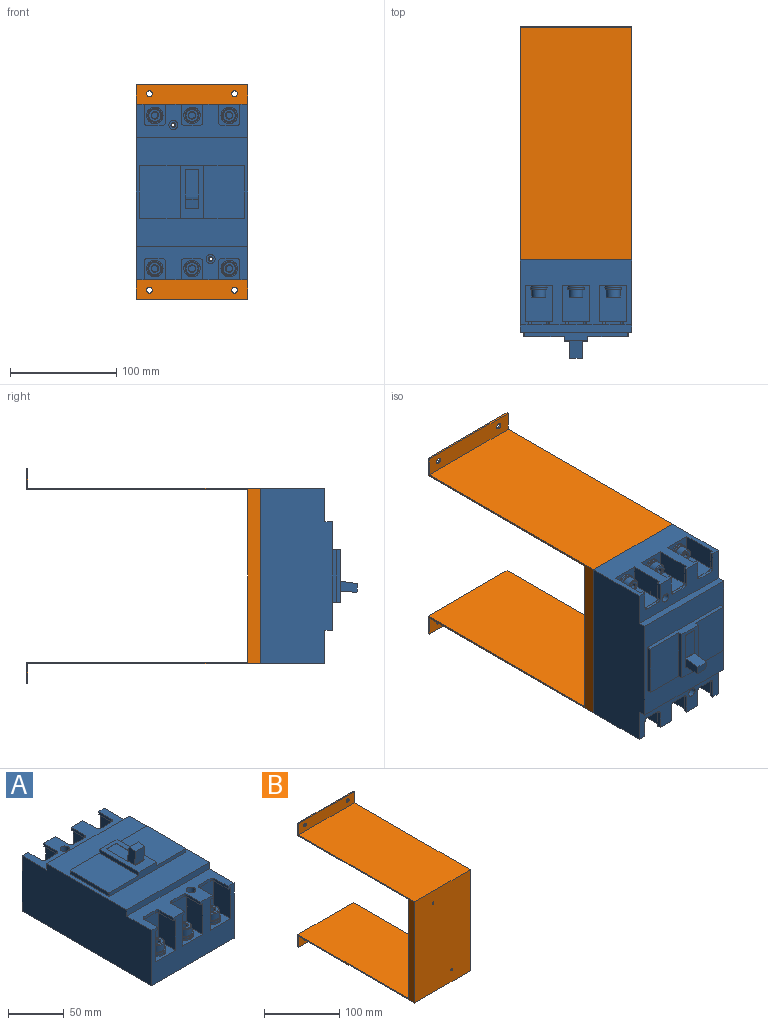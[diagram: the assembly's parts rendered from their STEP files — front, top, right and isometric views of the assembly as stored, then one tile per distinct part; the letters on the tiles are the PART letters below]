
ASSEMBLY  parts=2 mates=1
PART A: 239 faces, bbox 105x165x92 mm
  f0: plane 49x4mm, normal (1,0,0), area 196mm2, adj f1,f7,f8,f222
  f1: plane 4x0.5mm, normal (0.71,-0.71,0), area 2.8mm2, adj f0,f5,f7,f222
  f2: plane 49x4mm, normal (-1,0,0), area 196mm2, adj f3,f4,f222,f223
  f3: plane 50x38mm, normal (0,0,1), area 1899.8mm2, adj f2,f4,f5,f223,f224,f225
  f4: plane 4x0.5mm, normal (-0.71,-0.71,0), area 2.8mm2, adj f2,f3,f5,f222
  f5: plane 97x8mm, normal (0,-1,0), area 476mm2, adj f1,f3,f4,f6,f7,f222,f225,f226
  f6: plane 50x4mm, normal (1,0,0), area 200mm2, adj f5,f7,f224,f226
  f7: plane 50x38mm, normal (0,0,1), area 1899.8mm2, adj f0,f1,f5,f6,f8,f224
  f8: plane 4x0.5mm, normal (0.71,0.71,0), area 2.8mm2, adj f0,f7,f222,f224
  f9: plane 6.93x6mm, normal (0,0,1), area 31.2mm2, adj f10,f11,f12,f13,f14,f15
  f10: plane 6.98x3mm, normal (-0.5,0.87,0), area 23.1mm2, adj f9,f11,f15,f16
  f11: plane 6.98x3.46mm, normal (-1,0,0), area 23.1mm2, adj f9,f10,f12,f16
  f12: plane 6.98x3mm, normal (-0.5,-0.87,0), area 23.1mm2, adj f9,f11,f13,f16
  f13: plane 6.98x3mm, normal (0.5,-0.87,0), area 23.1mm2, adj f9,f12,f14,f16
  f14: plane 6.98x3.46mm, normal (1,0,0), area 23.1mm2, adj f9,f13,f15,f16
  f15: plane 6.98x3mm, normal (0.5,0.87,0), area 23.1mm2, adj f9,f10,f14,f16
  f16: cone r=2.46mm half-angle=45deg, axis (0,0,1), area 9.7mm2, adj f10,f11,f12,f13,f14,f15,f17
  f17: plane 11.4x11.4mm, normal (0,0,1), area 64mm2, adj f16,f18
  f18: cone r=5.7mm half-angle=45deg, axis (0,0,-1), area 43.4mm2, adj f17,f19
  f19: cylinder r=6.5mm len=13mm, axis (0,0,-1), area 294.1mm2, adj f18,f20,f24
  f20: plane 15.4x15.4mm, normal (0,0,1), area 53.3mm2, adj f19,f21,f22,f29
  f21: cylinder r=7.7mm len=15.4mm, axis (0,0,1), area 96.3mm2, adj f20,f22,f29,f30
  f22: plane 3.62x2mm, normal (0,-0.97,-0.26), area 7.5mm2, adj f20,f21,f23,f24,f28,f30
  f23: cylinder r=4.1mm len=8.2mm, axis (0,0,-1), area 51.1mm2, adj f22,f24,f28,f29
  f24: plane 10.6x8.2mm, normal (0,0,-1), area 3mm2, adj f19,f22,f23,f25,f29
  f25: cylinder r=4mm len=8mm, axis (0,0,-1), area 90.5mm2, adj f24,f26
  f26: plane 8.4x8.4mm, normal (0,0,1), area 5.2mm2, adj f25,f27
  f27: cylinder r=4.2mm len=8.4mm, axis (0,0,1), area 42.2mm2, adj f26,f28,f30
  f28: plane 8.4x8.4mm, normal (0,0,-1), area 2.6mm2, adj f22,f23,f27,f29
  f29: plane 3.62x2mm, normal (0,0.97,0.26), area 7.5mm2, adj f20,f21,f23,f24,f28,f30
  f30: plane 15.5x15.5mm, normal (0,0,1), area 3.2mm2, adj f21,f22,f27,f29,f31
  f31: cylinder r=7.75mm len=15.5mm, axis (0,0,-1), area 77.9mm2, adj f30,f34
  f32: plane 34x25.5mm, normal (0,1,0), area 867mm2, adj f33,f34,f35,f40
  f33: plane 34x21mm, normal (1,0,0), area 714mm2, adj f32,f34,f40,f214
  f34: plane 25.5x21mm, normal (0,0,1), area 346.8mm2, adj f31,f32,f33,f35,f214
  f35: plane 34x21mm, normal (-1,0,0), area 714mm2, adj f32,f34,f40,f214
  f36: cylinder r=3mm len=3mm, axis (0,0,-1), area 14.1mm2, adj f39,f40,f41,f219
  f37: plane 17x3mm, normal (-1,0,0), area 51mm2, adj f38,f40,f214,f219
  f38: cylinder r=3mm len=3mm, axis (0,0,1), area 14.1mm2, adj f37,f39,f40,f219
  f39: plane 14x3mm, normal (0,1,0), area 42mm2, adj f36,f38,f40,f219
  f40: plane 25.5x21mm, normal (0,0,-1), area 139.4mm2, adj f32,f33,f35,f36,f37,f38,f39,f41
  f41: plane 17x3mm, normal (1,0,0), area 51mm2, adj f36,f40,f214,f219
  f42: plane 6.93x6mm, normal (0,0,1), area 31.2mm2, adj f43,f44,f45,f46,f47,f48
  f43: plane 6.98x3mm, normal (-0.5,0.87,0), area 23.1mm2, adj f42,f44,f48,f49
  f44: plane 6.98x3.46mm, normal (-1,0,0), area 23.1mm2, adj f42,f43,f45,f49
  f45: plane 6.98x3mm, normal (-0.5,-0.87,0), area 23.1mm2, adj f42,f44,f46,f49
  f46: plane 6.98x3mm, normal (0.5,-0.87,0), area 23.1mm2, adj f42,f45,f47,f49
  f47: plane 6.98x3.46mm, normal (1,0,0), area 23.1mm2, adj f42,f46,f48,f49
  f48: plane 6.98x3mm, normal (0.5,0.87,0), area 23.1mm2, adj f42,f43,f47,f49
  f49: cone r=2.46mm half-angle=45deg, axis (0,0,1), area 9.7mm2, adj f43,f44,f45,f46,f47,f48,f50
  f50: plane 11.4x11.4mm, normal (0,0,1), area 64mm2, adj f49,f51
  f51: cone r=5.7mm half-angle=45deg, axis (0,0,-1), area 43.4mm2, adj f50,f52
  f52: cylinder r=6.5mm len=13mm, axis (0,0,-1), area 294.1mm2, adj f51,f53,f57
  f53: plane 15.4x15.4mm, normal (0,0,1), area 53.3mm2, adj f52,f54,f55,f62
  f54: cylinder r=7.7mm len=15.4mm, axis (0,0,1), area 96.3mm2, adj f53,f55,f62,f63
  f55: plane 3.62x2mm, normal (0,-0.97,-0.26), area 7.5mm2, adj f53,f54,f56,f57,f61,f63
  f56: cylinder r=4.1mm len=8.2mm, axis (0,0,-1), area 51.1mm2, adj f55,f57,f61,f62
  f57: plane 10.6x8.2mm, normal (0,0,-1), area 3mm2, adj f52,f55,f56,f58,f62
  f58: cylinder r=4mm len=8mm, axis (0,0,-1), area 90.5mm2, adj f57,f59
  f59: plane 8.4x8.4mm, normal (0,0,1), area 5.2mm2, adj f58,f60
  f60: cylinder r=4.2mm len=8.4mm, axis (0,0,1), area 42.2mm2, adj f59,f61,f63
  f61: plane 8.4x8.4mm, normal (0,0,-1), area 2.6mm2, adj f55,f56,f60,f62
  f62: plane 3.62x2mm, normal (0,0.97,0.26), area 7.5mm2, adj f53,f54,f56,f57,f61,f63
  f63: plane 15.5x15.5mm, normal (0,0,1), area 3.2mm2, adj f54,f55,f60,f62,f64
  f64: cylinder r=7.75mm len=15.5mm, axis (0,0,-1), area 77.9mm2, adj f63,f67
  f65: plane 34x25.5mm, normal (0,1,0), area 867mm2, adj f66,f67,f68,f69
  f66: plane 34x21mm, normal (1,0,0), area 714mm2, adj f65,f67,f69,f214
  f67: plane 25.5x21mm, normal (0,0,1), area 346.8mm2, adj f64,f65,f66,f68,f214
  f68: plane 34x21mm, normal (-1,0,0), area 714mm2, adj f65,f67,f69,f214
  f69: plane 25.5x21mm, normal (0,0,-1), area 139.4mm2, adj f65,f66,f68,f70,f214,f215,f216,f217
  f70: plane 17x3mm, normal (1,0,0), area 51mm2, adj f69,f214,f218,f219
  f71: plane 6.93x6mm, normal (0,0,1), area 31.2mm2, adj f72,f73,f74,f75,f76,f77
  f72: plane 6.98x3mm, normal (-0.5,0.87,0), area 23.1mm2, adj f71,f73,f77,f78
  f73: plane 6.98x3.46mm, normal (-1,0,0), area 23.1mm2, adj f71,f72,f74,f78
  f74: plane 6.98x3mm, normal (-0.5,-0.87,0), area 23.1mm2, adj f71,f73,f75,f78
  f75: plane 6.98x3mm, normal (0.5,-0.87,0), area 23.1mm2, adj f71,f74,f76,f78
  f76: plane 6.98x3.46mm, normal (1,0,0), area 23.1mm2, adj f71,f75,f77,f78
  f77: plane 6.98x3mm, normal (0.5,0.87,0), area 23.1mm2, adj f71,f72,f76,f78
  f78: cone r=2.46mm half-angle=45deg, axis (0,0,1), area 9.7mm2, adj f72,f73,f74,f75,f76,f77,f79
  f79: plane 11.4x11.4mm, normal (0,0,1), area 64mm2, adj f78,f80
  f80: cone r=5.7mm half-angle=45deg, axis (0,0,-1), area 43.4mm2, adj f79,f81
  f81: cylinder r=6.5mm len=13mm, axis (0,0,-1), area 294.1mm2, adj f80,f82,f86
  f82: plane 15.4x15.4mm, normal (0,0,1), area 53.3mm2, adj f81,f83,f84,f91
  f83: cylinder r=7.7mm len=15.4mm, axis (0,0,1), area 96.3mm2, adj f82,f84,f91,f92
  f84: plane 3.62x2mm, normal (0,-0.97,-0.26), area 7.5mm2, adj f82,f83,f85,f86,f90,f92
  f85: cylinder r=4.1mm len=8.2mm, axis (0,0,-1), area 51.1mm2, adj f84,f86,f90,f91
  f86: plane 10.6x8.2mm, normal (0,0,-1), area 3mm2, adj f81,f84,f85,f87,f91
  f87: cylinder r=4mm len=8mm, axis (0,0,-1), area 90.5mm2, adj f86,f88
  f88: plane 8.4x8.4mm, normal (0,0,1), area 5.2mm2, adj f87,f89
  f89: cylinder r=4.2mm len=8.4mm, axis (0,0,1), area 42.2mm2, adj f88,f90,f92
  f90: plane 8.4x8.4mm, normal (0,0,-1), area 2.6mm2, adj f84,f85,f89,f91
  f91: plane 3.62x2mm, normal (0,0.97,0.26), area 7.5mm2, adj f82,f83,f85,f86,f90,f92
  f92: plane 15.5x15.5mm, normal (0,0,1), area 3.2mm2, adj f83,f84,f89,f91,f93
  f93: cylinder r=7.75mm len=15.5mm, axis (0,0,-1), area 77.9mm2, adj f92,f96
  f94: plane 34x25.5mm, normal (0,-1,0), area 867mm2, adj f95,f96,f97,f102
  f95: plane 34x21mm, normal (-1,0,0), area 714mm2, adj f94,f96,f102,f173
  f96: plane 25.5x21mm, normal (0,0,1), area 346.8mm2, adj f93,f94,f95,f97,f173
  f97: plane 34x21mm, normal (1,0,0), area 714mm2, adj f94,f96,f102,f173
  f98: cylinder r=3mm len=3mm, axis (0,0,-1), area 14.1mm2, adj f101,f102,f103,f178
  f99: plane 17x3mm, normal (1,0,0), area 51mm2, adj f100,f102,f173,f178
  f100: cylinder r=3mm len=3mm, axis (0,0,1), area 14.1mm2, adj f99,f101,f102,f178
  f101: plane 14x3mm, normal (0,-1,0), area 42mm2, adj f98,f100,f102,f178
  f102: plane 25.5x21mm, normal (0,0,-1), area 139.4mm2, adj f94,f95,f97,f98,f99,f100,f101,f103
  f103: plane 17x3mm, normal (-1,0,0), area 51mm2, adj f98,f102,f173,f178
  f104: plane 6.93x6mm, normal (0,0,1), area 31.2mm2, adj f105,f106,f107,f108,f109,f110
  f105: plane 6.98x3mm, normal (-0.5,0.87,0), area 23.1mm2, adj f104,f106,f110,f111
  f106: plane 6.98x3.46mm, normal (-1,0,0), area 23.1mm2, adj f104,f105,f107,f111
  f107: plane 6.98x3mm, normal (-0.5,-0.87,0), area 23.1mm2, adj f104,f106,f108,f111
  f108: plane 6.98x3mm, normal (0.5,-0.87,0), area 23.1mm2, adj f104,f107,f109,f111
  f109: plane 6.98x3.46mm, normal (1,0,0), area 23.1mm2, adj f104,f108,f110,f111
  f110: plane 6.98x3mm, normal (0.5,0.87,0), area 23.1mm2, adj f104,f105,f109,f111
  f111: cone r=2.46mm half-angle=45deg, axis (0,0,1), area 9.7mm2, adj f105,f106,f107,f108,f109,f110,f112
  f112: plane 11.4x11.4mm, normal (0,0,1), area 64mm2, adj f111,f113
  f113: cone r=5.7mm half-angle=45deg, axis (0,0,-1), area 43.4mm2, adj f112,f114
  f114: cylinder r=6.5mm len=13mm, axis (0,0,-1), area 294.1mm2, adj f113,f115,f119
  f115: plane 15.4x15.4mm, normal (0,0,1), area 53.3mm2, adj f114,f116,f117,f124
  f116: cylinder r=7.7mm len=15.4mm, axis (0,0,1), area 96.3mm2, adj f115,f117,f124,f125
  f117: plane 3.62x2mm, normal (0,-0.97,-0.26), area 7.5mm2, adj f115,f116,f118,f119,f123,f125
  f118: cylinder r=4.1mm len=8.2mm, axis (0,0,-1), area 51.1mm2, adj f117,f119,f123,f124
  f119: plane 10.6x8.2mm, normal (0,0,-1), area 3mm2, adj f114,f117,f118,f120,f124
  f120: cylinder r=4mm len=8mm, axis (0,0,-1), area 90.5mm2, adj f119,f121
  f121: plane 8.4x8.4mm, normal (0,0,1), area 5.2mm2, adj f120,f122
  f122: cylinder r=4.2mm len=8.4mm, axis (0,0,1), area 42.2mm2, adj f121,f123,f125
  f123: plane 8.4x8.4mm, normal (0,0,-1), area 2.6mm2, adj f117,f118,f122,f124
  f124: plane 3.62x2mm, normal (0,0.97,0.26), area 7.5mm2, adj f115,f116,f118,f119,f123,f125
  f125: plane 15.5x15.5mm, normal (0,0,1), area 3.2mm2, adj f116,f117,f122,f124,f126
  f126: cylinder r=7.75mm len=15.5mm, axis (0,0,-1), area 77.9mm2, adj f125,f129
  f127: plane 34x25.5mm, normal (0,-1,0), area 867mm2, adj f128,f129,f130,f131
  f128: plane 34x21mm, normal (-1,0,0), area 714mm2, adj f127,f129,f131,f173
  f129: plane 25.5x21mm, normal (0,0,1), area 346.8mm2, adj f126,f127,f128,f130,f173
  f130: plane 34x21mm, normal (1,0,0), area 714mm2, adj f127,f129,f131,f173
  f131: plane 25.5x21mm, normal (0,0,-1), area 139.4mm2, adj f127,f128,f130,f132,f173,f174,f175,f176
  f132: plane 17x3mm, normal (-1,0,0), area 51mm2, adj f131,f173,f177,f178
  f133: cylinder r=4.25mm len=16mm, axis (0,0,-1), area 427.3mm2, adj f134,f219
  f134: plane 8.5x8.5mm, normal (0,0,1), area 40.8mm2, adj f133,f135
  f135: cylinder r=2.25mm len=45mm, axis (0,0,-1), area 636.2mm2, adj f134,f139
  f136: cylinder r=4.25mm len=16mm, axis (0,0,-1), area 427.3mm2, adj f137,f178
  f137: plane 8.5x8.5mm, normal (0,0,1), area 40.8mm2, adj f136,f138
  f138: cylinder r=2.25mm len=45mm, axis (0,0,-1), area 636.2mm2, adj f137,f139
  f139: plane 165x105mm, normal (0,0,-1), area 17293.2mm2, adj f135,f138,f173,f180,f214,f221
  f140: plane 6.93x6mm, normal (0,0,1), area 31.2mm2, adj f141,f142,f143,f144,f145,f146
  f141: plane 6.98x3mm, normal (-0.5,0.87,0), area 23.1mm2, adj f140,f142,f146,f147
  f142: plane 6.98x3.46mm, normal (-1,0,0), area 23.1mm2, adj f140,f141,f143,f147
  f143: plane 6.98x3mm, normal (-0.5,-0.87,0), area 23.1mm2, adj f140,f142,f144,f147
  f144: plane 6.98x3mm, normal (0.5,-0.87,0), area 23.1mm2, adj f140,f143,f145,f147
  f145: plane 6.98x3.46mm, normal (1,0,0), area 23.1mm2, adj f140,f144,f146,f147
  f146: plane 6.98x3mm, normal (0.5,0.87,0), area 23.1mm2, adj f140,f141,f145,f147
  f147: cone r=2.46mm half-angle=45deg, axis (0,0,1), area 9.7mm2, adj f141,f142,f143,f144,f145,f146,f148
  f148: plane 11.4x11.4mm, normal (0,0,1), area 64mm2, adj f147,f149
  f149: cone r=5.7mm half-angle=45deg, axis (0,0,-1), area 43.4mm2, adj f148,f150
  f150: cylinder r=6.5mm len=13mm, axis (0,0,-1), area 294.1mm2, adj f149,f151,f155
  f151: plane 15.4x15.4mm, normal (0,0,1), area 53.3mm2, adj f150,f152,f153,f160
  f152: cylinder r=7.7mm len=15.4mm, axis (0,0,1), area 96.3mm2, adj f151,f153,f160,f161
  f153: plane 3.62x2mm, normal (0,-0.97,-0.26), area 7.5mm2, adj f151,f152,f154,f155,f159,f161
  f154: cylinder r=4.1mm len=8.2mm, axis (0,0,-1), area 51.1mm2, adj f153,f155,f159,f160
  f155: plane 10.6x8.2mm, normal (0,0,-1), area 3mm2, adj f150,f153,f154,f156,f160
  f156: cylinder r=4mm len=8mm, axis (0,0,-1), area 90.5mm2, adj f155,f157
  f157: plane 8.4x8.4mm, normal (0,0,1), area 5.2mm2, adj f156,f158
  f158: cylinder r=4.2mm len=8.4mm, axis (0,0,1), area 42.2mm2, adj f157,f159,f161
  f159: plane 8.4x8.4mm, normal (0,0,-1), area 2.6mm2, adj f153,f154,f158,f160
  f160: plane 3.62x2mm, normal (0,0.97,0.26), area 7.5mm2, adj f151,f152,f154,f155,f159,f161
  f161: plane 15.5x15.5mm, normal (0,0,1), area 3.2mm2, adj f152,f153,f158,f160,f162
  f162: cylinder r=7.75mm len=15.5mm, axis (0,0,-1), area 77.9mm2, adj f161,f172
  f163: plane 34x21mm, normal (-1,0,0), area 714mm2, adj f169,f170,f172,f173
  f164: plane 17x3mm, normal (-1,0,0), area 51mm2, adj f165,f169,f173,f178
  f165: cylinder r=3mm len=3mm, axis (0,0,-1), area 14.1mm2, adj f164,f168,f169,f178
  f166: plane 17x3mm, normal (1,0,0), area 51mm2, adj f167,f169,f173,f178
  f167: cylinder r=3mm len=3mm, axis (0,0,1), area 14.1mm2, adj f166,f168,f169,f178
  f168: plane 14x3mm, normal (0,-1,0), area 42mm2, adj f165,f167,f169,f178
  f169: plane 25.5x21mm, normal (0,0,-1), area 139.4mm2, adj f163,f164,f165,f166,f167,f168,f170,f171
  f170: plane 34x25.5mm, normal (0,-1,0), area 867mm2, adj f163,f169,f171,f172
  f171: plane 34x21mm, normal (1,0,0), area 714mm2, adj f169,f170,f172,f173
  f172: plane 25.5x21mm, normal (0,0,1), area 346.8mm2, adj f162,f163,f170,f171,f173
  f173: plane 105x61mm, normal (0,-1,0), area 3624mm2, adj f95,f96,f97,f99,f102,f103,f128,f129
  f174: plane 17x3mm, normal (1,0,0), area 51mm2, adj f131,f173,f175,f178
  f175: cylinder r=3mm len=3mm, axis (0,0,1), area 14.1mm2, adj f131,f174,f176,f178
  f176: plane 14x3mm, normal (0,-1,0), area 42mm2, adj f131,f175,f177,f178
  f177: cylinder r=3mm len=3mm, axis (0,0,-1), area 14.1mm2, adj f131,f132,f176,f178
  f178: plane 105x31.5mm, normal (0,0,1), area 2062.3mm2, adj f98,f99,f100,f101,f103,f132,f136,f164
  f179: plane 105x7mm, normal (0,-1,0), area 735mm2, adj f178,f180,f221,f222
  f180: plane 165x68mm, normal (1,0,0), area 10779mm2, adj f139,f173,f178,f179,f214,f219,f220,f222
  f181: plane 6.93x6mm, normal (0,0,1), area 31.2mm2, adj f182,f183,f184,f185,f186,f187
  f182: plane 6.98x3mm, normal (-0.5,0.87,0), area 23.1mm2, adj f181,f183,f187,f188
  f183: plane 6.98x3.46mm, normal (-1,0,0), area 23.1mm2, adj f181,f182,f184,f188
  f184: plane 6.98x3mm, normal (-0.5,-0.87,0), area 23.1mm2, adj f181,f183,f185,f188
  f185: plane 6.98x3mm, normal (0.5,-0.87,0), area 23.1mm2, adj f181,f184,f186,f188
  f186: plane 6.98x3.46mm, normal (1,0,0), area 23.1mm2, adj f181,f185,f187,f188
  f187: plane 6.98x3mm, normal (0.5,0.87,0), area 23.1mm2, adj f181,f182,f186,f188
  f188: cone r=2.46mm half-angle=45deg, axis (0,0,1), area 9.7mm2, adj f182,f183,f184,f185,f186,f187,f189
  f189: plane 11.4x11.4mm, normal (0,0,1), area 64mm2, adj f188,f190
  f190: cone r=5.7mm half-angle=45deg, axis (0,0,-1), area 43.4mm2, adj f189,f191
  f191: cylinder r=6.5mm len=13mm, axis (0,0,-1), area 294.1mm2, adj f190,f192,f196
  f192: plane 15.4x15.4mm, normal (0,0,1), area 53.3mm2, adj f191,f193,f194,f201
  f193: cylinder r=7.7mm len=15.4mm, axis (0,0,1), area 96.3mm2, adj f192,f194,f201,f202
  f194: plane 3.62x2mm, normal (0,-0.97,-0.26), area 7.5mm2, adj f192,f193,f195,f196,f200,f202
  f195: cylinder r=4.1mm len=8.2mm, axis (0,0,-1), area 51.1mm2, adj f194,f196,f200,f201
  f196: plane 10.6x8.2mm, normal (0,0,-1), area 3mm2, adj f191,f194,f195,f197,f201
  f197: cylinder r=4mm len=8mm, axis (0,0,-1), area 90.5mm2, adj f196,f198
  f198: plane 8.4x8.4mm, normal (0,0,1), area 5.2mm2, adj f197,f199
  f199: cylinder r=4.2mm len=8.4mm, axis (0,0,1), area 42.2mm2, adj f198,f200,f202
  f200: plane 8.4x8.4mm, normal (0,0,-1), area 2.6mm2, adj f194,f195,f199,f201
  f201: plane 3.62x2mm, normal (0,0.97,0.26), area 7.5mm2, adj f192,f193,f195,f196,f200,f202
  f202: plane 15.5x15.5mm, normal (0,0,1), area 3.2mm2, adj f193,f194,f199,f201,f203
  f203: cylinder r=7.75mm len=15.5mm, axis (0,0,-1), area 77.9mm2, adj f202,f213
  f204: plane 34x21mm, normal (1,0,0), area 714mm2, adj f210,f211,f213,f214
  f205: plane 17x3mm, normal (1,0,0), area 51mm2, adj f206,f210,f214,f219
  f206: cylinder r=3mm len=3mm, axis (0,0,-1), area 14.1mm2, adj f205,f209,f210,f219
  f207: plane 17x3mm, normal (-1,0,0), area 51mm2, adj f208,f210,f214,f219
  f208: cylinder r=3mm len=3mm, axis (0,0,1), area 14.1mm2, adj f207,f209,f210,f219
  f209: plane 14x3mm, normal (0,1,0), area 42mm2, adj f206,f208,f210,f219
  f210: plane 25.5x21mm, normal (0,0,-1), area 139.4mm2, adj f204,f205,f206,f207,f208,f209,f211,f212
  f211: plane 34x25.5mm, normal (0,1,0), area 867mm2, adj f204,f210,f212,f213
  f212: plane 34x21mm, normal (-1,0,0), area 714mm2, adj f210,f211,f213,f214
  f213: plane 25.5x21mm, normal (0,0,1), area 346.8mm2, adj f203,f204,f211,f212,f214
  f214: plane 105x61mm, normal (0,1,0), area 3624mm2, adj f33,f34,f35,f37,f40,f41,f66,f67
  f215: plane 17x3mm, normal (-1,0,0), area 51mm2, adj f69,f214,f216,f219
  f216: cylinder r=3mm len=3mm, axis (0,0,1), area 14.1mm2, adj f69,f215,f217,f219
  f217: plane 14x3mm, normal (0,1,0), area 42mm2, adj f69,f216,f218,f219
  f218: cylinder r=3mm len=3mm, axis (0,0,-1), area 14.1mm2, adj f69,f70,f217,f219
  f219: plane 105x31.5mm, normal (0,0,1), area 2062.3mm2, adj f36,f37,f38,f39,f41,f70,f133,f180
  f220: plane 105x7mm, normal (0,1,0), area 735mm2, adj f180,f219,f221,f222
  f221: plane 165x68mm, normal (-1,0,0), area 10779mm2, adj f139,f173,f178,f179,f214,f219,f220,f222
  f222: plane 105x102mm, normal (0,0,1), area 5810.5mm2, adj f0,f1,f2,f4,f5,f8,f179,f180
  f223: plane 4x0.5mm, normal (-0.71,0.71,0), area 2.8mm2, adj f2,f3,f222,f224
  f224: plane 97x8mm, normal (0,1,0), area 476mm2, adj f3,f6,f7,f8,f222,f223,f225,f226
  f225: plane 50x4mm, normal (-1,0,0), area 200mm2, adj f3,f5,f224,f226
  f226: plane 50x22mm, normal (0,0,1), area 645.3mm2, adj f5,f6,f224,f225,f227,f228,f229,f230
  f227: plane 36.67x0.5mm, normal (1,0,0), area 18.3mm2, adj f226,f228,f230,f231
  f228: plane 12.4x0.5mm, normal (0,-1,0), area 6.2mm2, adj f226,f227,f229,f231
  f229: plane 36.67x0.5mm, normal (-1,0,0), area 18.3mm2, adj f226,f228,f230,f231
  f230: plane 12.4x0.5mm, normal (0,1,0), area 6.2mm2, adj f226,f227,f229,f231
  f231: plane 36.67x12.4mm, normal (0,0,1), area 345.9mm2, adj f227,f228,f229,f230,f234,f235,f237,f238
  f232: plane 11.6x8.21mm, normal (0,-0.1,0.99), area 95.8mm2, adj f233,f234,f236,f237
  f233: plane 16x11.6mm, normal (0,0.99,0.14), area 187.4mm2, adj f232,f234,f237,f238
  f234: plane 16.5x10.45mm, normal (1,0,0), area 142.3mm2, adj f231,f232,f233,f235,f236,f238
  f235: plane 11.6x0.5mm, normal (0,-1,0), area 5.8mm2, adj f231,f234,f236,f237
  f236: plane 15.14x11.6mm, normal (0,-1,-0.07), area 176mm2, adj f232,f234,f235,f237
  f237: plane 16.5x10.45mm, normal (-1,0,0), area 142.3mm2, adj f231,f232,f233,f235,f236,f238
  f238: plane 11.6x0.5mm, normal (0,1,0), area 5.8mm2, adj f231,f233,f234,f237
PART B: 24 faces, bbox 105x220x201.8 mm
  f0: plane 161.8x101.8mm, normal (0,1,0), area 16454.1mm2, adj f1,f11,f14,f16,f18,f19
  f1: plane 218.4x105mm, normal (0,0,-1), area 22900mm2, adj f0,f2,f12,f13,f14,f15,f16,f17
  f2: plane 105x20mm, normal (0,1,0), area 2052.5mm2, adj f1,f3,f12,f13,f22,f23
  f3: plane 105x1.6mm, normal (0,0,1), area 168mm2, adj f2,f4,f12,f13
  f4: plane 105x18.4mm, normal (0,-1,0), area 1884.5mm2, adj f3,f5,f12,f13,f22,f23
  f5: plane 218.4x105mm, normal (0,0,1), area 22932mm2, adj f4,f6,f12,f13
  f6: plane 165x105mm, normal (0,-1,0), area 17307.9mm2, adj f5,f7,f12,f13,f18,f19
  f7: plane 218.4x105mm, normal (0,0,-1), area 22932mm2, adj f6,f8,f12,f13
  f8: plane 105x18.4mm, normal (0,-1,0), area 1884.5mm2, adj f7,f9,f12,f13,f20,f21
  f9: plane 105x1.6mm, normal (0,0,-1), area 168mm2, adj f8,f10,f12,f13
  f10: plane 105x20mm, normal (0,1,0), area 2052.5mm2, adj f9,f11,f12,f13,f20,f21
  f11: plane 218.4x105mm, normal (0,0,1), area 22900mm2, adj f0,f10,f12,f13,f14,f15,f16,f17
  f12: plane 220x201.8mm, normal (1,0,0), area 2639.8mm2, adj f1,f2,f3,f4,f5,f6,f7,f8
  f13: plane 220x201.8mm, normal (-1,0,0), area 2639.8mm2, adj f1,f2,f3,f4,f5,f6,f7,f8
  f14: plane 161.8x10mm, normal (-1,0,0), area 1618mm2, adj f0,f1,f11,f15
  f15: plane 161.8x1.6mm, normal (0,1,0), area 258.9mm2, adj f1,f11,f12,f14
  f16: plane 161.8x10mm, normal (1,0,0), area 1618mm2, adj f0,f1,f11,f17
  f17: plane 161.8x1.6mm, normal (0,1,0), area 258.9mm2, adj f1,f11,f13,f16
  f18: cylinder r=1.65mm len=3.3mm, axis (0,-1,0), area 16.6mm2, adj f0,f6
  f19: cylinder r=1.65mm len=3.3mm, axis (0,-1,0), area 16.6mm2, adj f0,f6
  f20: cylinder r=2.75mm len=5.5mm, axis (0,-1,0), area 27.6mm2, adj f8,f10
  f21: cylinder r=2.75mm len=5.5mm, axis (0,-1,0), area 27.6mm2, adj f8,f10
  f22: cylinder r=2.75mm len=5.5mm, axis (0,-1,0), area 27.6mm2, adj f2,f4
  f23: cylinder r=2.75mm len=5.5mm, axis (0,-1,0), area 27.6mm2, adj f2,f4
PLACE A rot(axis=(1,0,0),90deg) t=(-358.28,-173.79,-210.4)mm
PLACE B t=(-130.78,46.21,-311.3)mm
MATE slider A.f133 <-> B.f19  axis (0,1,0) through (-95.78,-173.79,-147.4)mm
